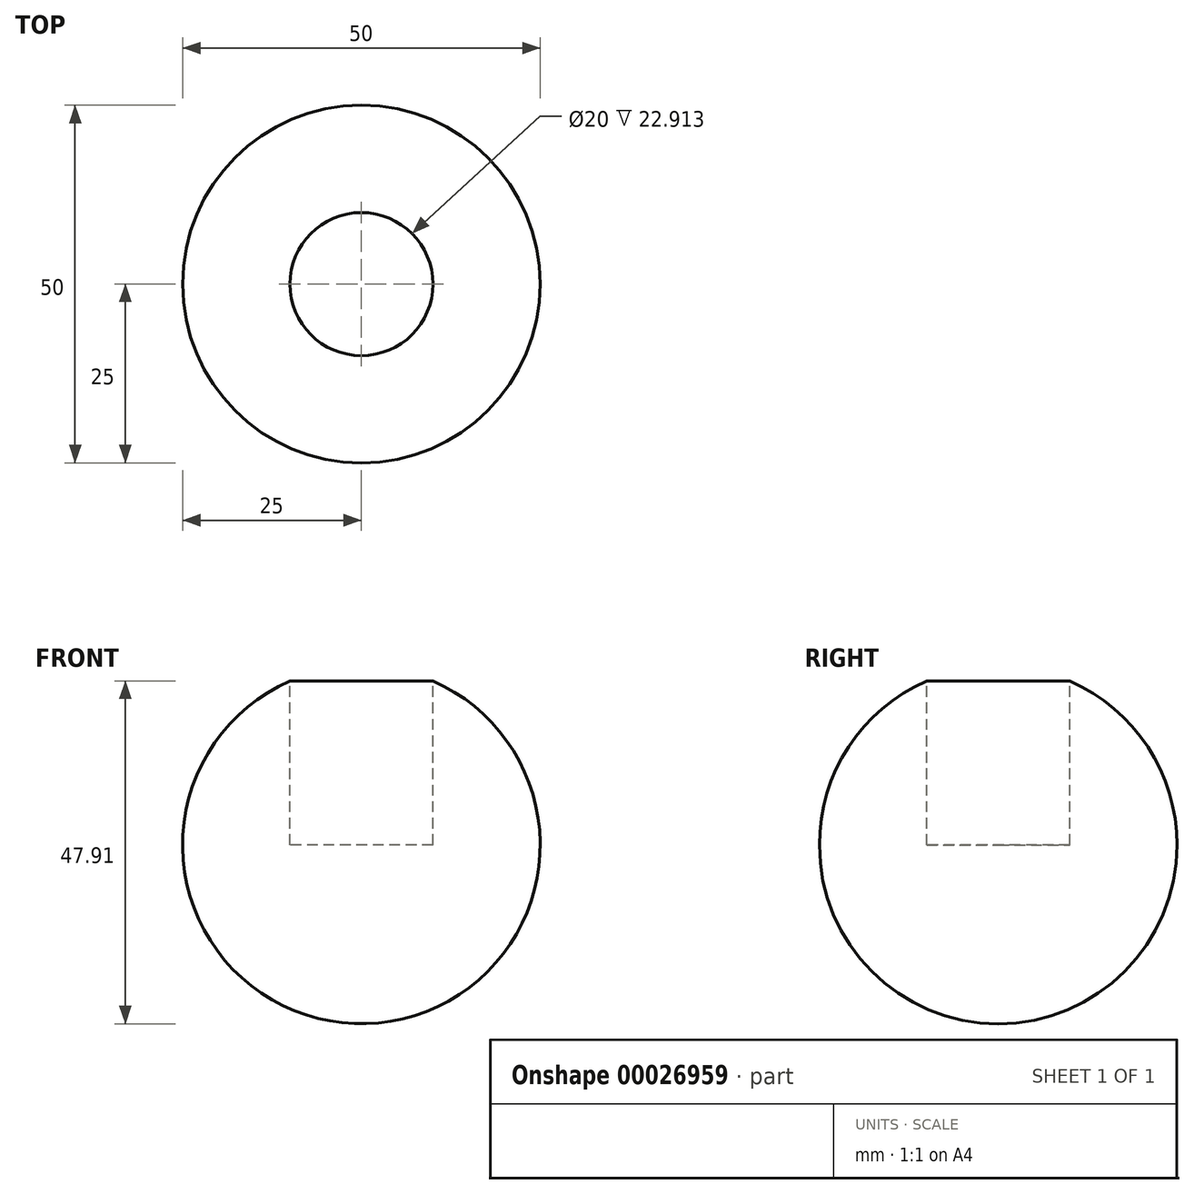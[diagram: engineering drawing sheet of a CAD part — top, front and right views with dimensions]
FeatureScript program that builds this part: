
annotation { "Feature Type Name" : "Feature", "Feature Type Description" : "" }
export const myFeature = defineFeature(function(context is Context, id is Id, definition is map)
    precondition{}
    {
        {
            var Q0;
            Q0=qCreatedBy(makeId("Top.planeOp"),FACE);
            var sketch = newSketch(context, id + "F0", { "sketchPlane" : qUnion([Q0])});
            skArc(sketch, "E0", {"start": v(0, -25) * mm, "mid": v(25, 0) * mm, "end": v(0, 25) * mm});
            skLineSegment(sketch, "E1", {"start": v(0, 25) * mm, "end": v(0, -25) * mm});
            skSolve(sketch);
        }
        {
            var Q0;
            Q0=makeQuery(id+"F0.imprint","IMPRINT",FACE,{"disambiguationData":[TD([[makeQuery(id+"F0.imprint","IMPRINT",EDGE,{"derivedFrom":sQuery(id+"F0.wireOp",EDGE,"E0")}),1.0]])]});
            var Q1;
            Q1=sQuery(id+"F0.wireOp",EDGE,"E1");
            revolve(context, id + "F1", {"entities" : qUnion([Q0]), "axis" : qUnion([Q1]), "revolveType" : RevolveType.FULL});
        }
        {
            var Q0;
            Q0=qCreatedBy(makeId("Top.planeOp"),FACE);
            cPlane(context, id + "F2", {"entities" : qUnion([Q0]), "cplaneType" : CPlaneType.OFFSET, "offset" : 25 * mm, "width" : 150 * mm, "height" : 150 * mm});
        }
        {
            var Q0;
            Q0=qCreatedBy(id+"F2.planeOp",FACE);
            var sketch = newSketch(context, id + "F3", { "sketchPlane" : qUnion([Q0])});
            skCircle(sketch, "E2", {"center": v(0, 0) * mm, "radius": 10 * mm});
            skSolve(sketch);
        }
        {
            var Q0;
            Q0=makeQuery(id+"F3.imprint","IMPRINT",FACE,{"disambiguationData":[TD([[makeQuery(id+"F3.imprint","IMPRINT",EDGE,{"derivedFrom":sQuery(id+"F3.wireOp",EDGE,"E2")}),1.0]])]});
            extrude(context, id + "F4", {"entities" : qUnion([Q0]), "operationType" : NewBodyOperationType.REMOVE, "oppositeDirection" : true, "depth" : 25 * mm});
        }
    });
